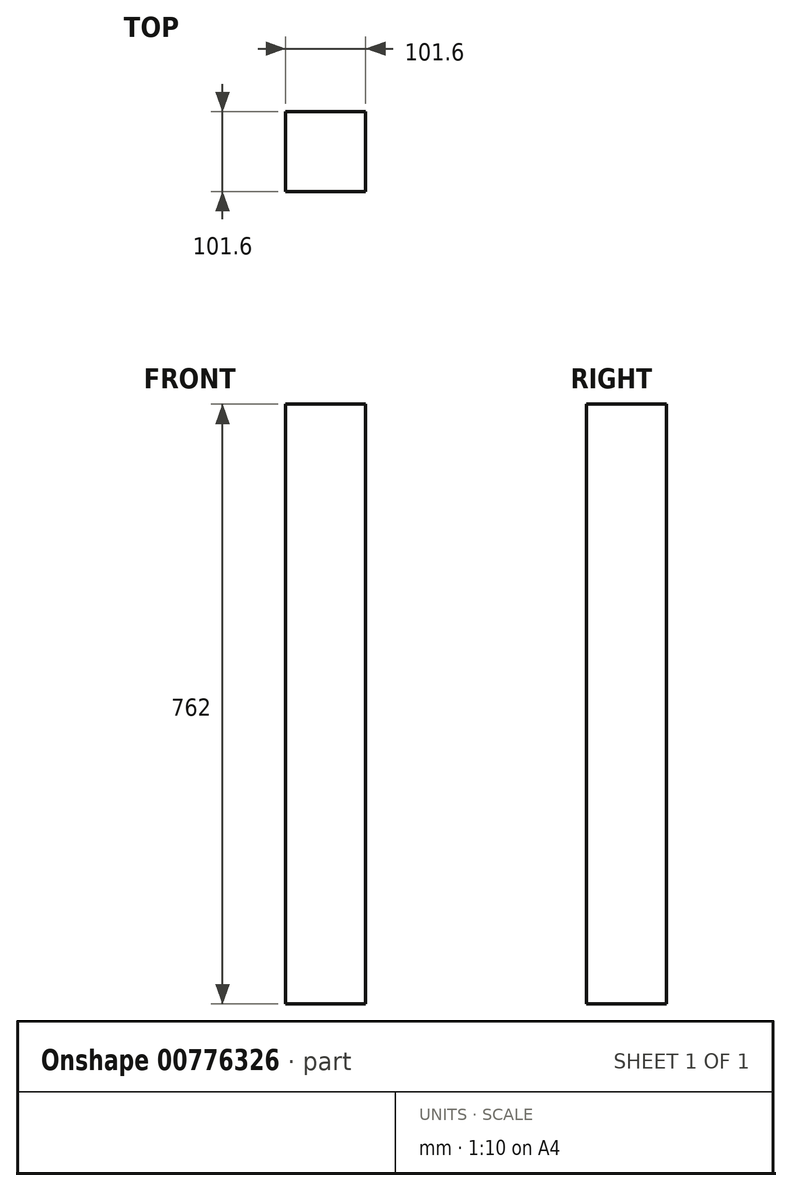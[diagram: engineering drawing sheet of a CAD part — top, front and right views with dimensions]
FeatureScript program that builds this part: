
annotation { "Feature Type Name" : "Feature", "Feature Type Description" : "" }
export const myFeature = defineFeature(function(context is Context, id is Id, definition is map)
    precondition{}
    {
        {
            var Q0;
            Q0=qCreatedBy(makeId("Top.planeOp"),FACE);
            var sketch = newSketch(context, id + "F0", { "sketchPlane" : qUnion([Q0])});
            skLineSegment(sketch, "E0.bottom", {"start": v(-50.8, 50.8) * mm, "end": v(50.8, 50.8) * mm});
            skLineSegment(sketch, "E0.top", {"start": v(-50.8, -50.8) * mm, "end": v(50.8, -50.8) * mm});
            skLineSegment(sketch, "E0.left", {"start": v(-50.8, 50.8) * mm, "end": v(-50.8, -50.8) * mm});
            skLineSegment(sketch, "E0.right", {"start": v(50.8, 50.8) * mm, "end": v(50.8, -50.8) * mm});
            skPoint(sketch, "E0.middle", {"position": v(0, 0) * mm});
            skSolve(sketch);
        }
        {
            var Q0;
            Q0=makeQuery(id+"F0.imprint","IMPRINT",FACE,{"disambiguationData":[TD([[makeQuery(id+"F0.imprint","IMPRINT",EDGE,{"derivedFrom":sQuery(id+"F0.wireOp",EDGE,"E0.bottom")}),-1.0]])]});
            extrude(context, id + "F1", {"entities" : qUnion([Q0]), "endBound" : BoundingType.SYMMETRIC, "depth" : 762 * mm, "offsetDistance" : 25.4 * mm});
        }
    });
